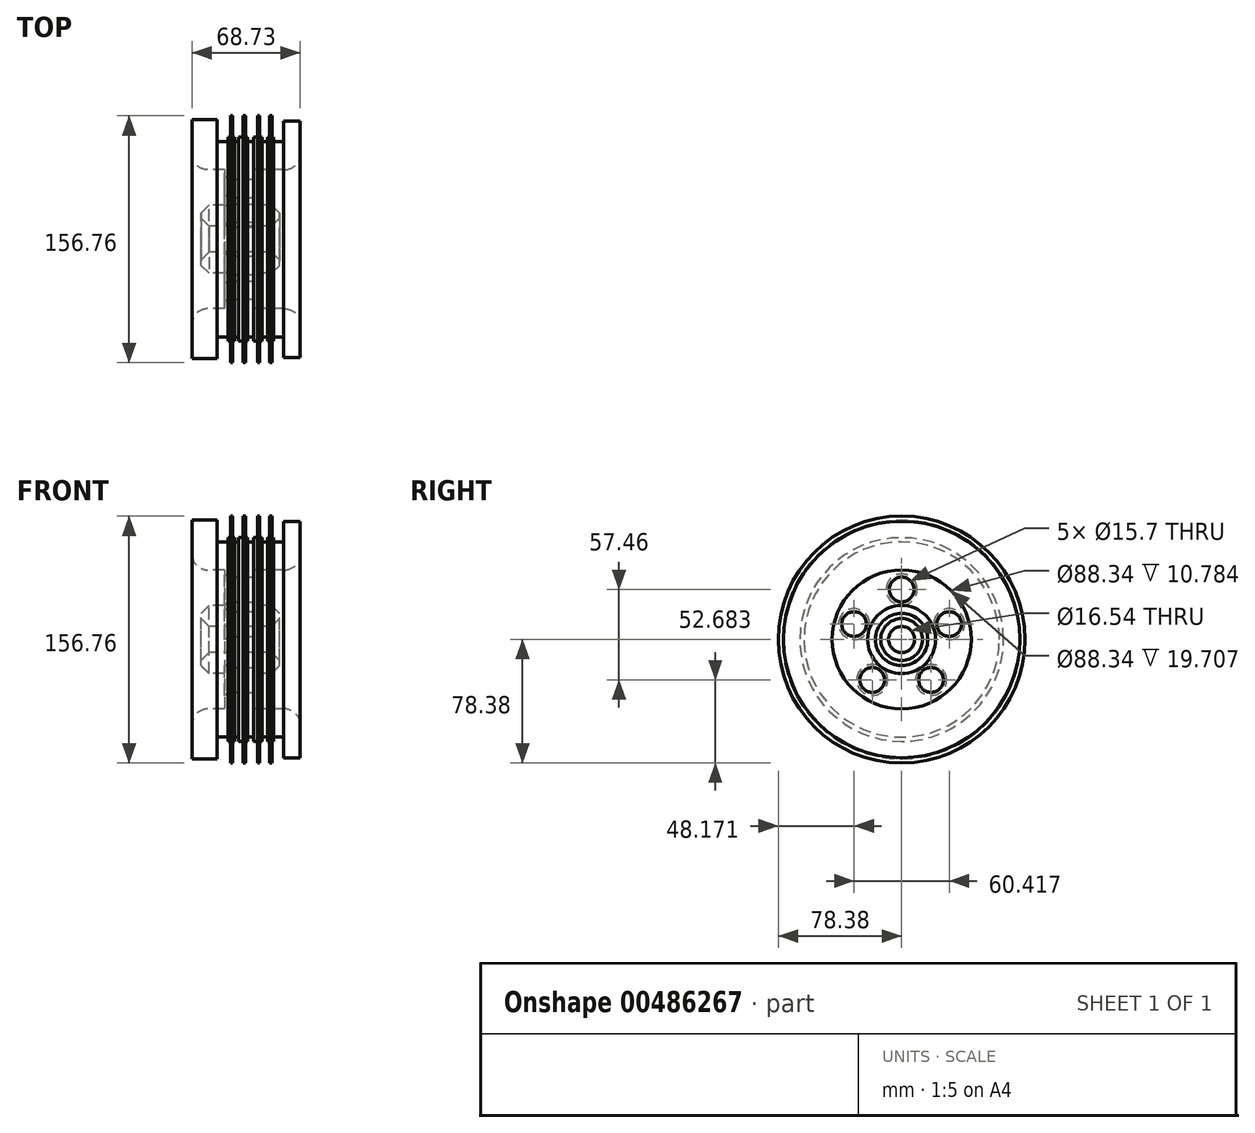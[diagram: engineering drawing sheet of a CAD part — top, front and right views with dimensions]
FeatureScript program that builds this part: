
annotation { "Feature Type Name" : "Feature", "Feature Type Description" : "" }
export const myFeature = defineFeature(function(context is Context, id is Id, definition is map)
    precondition{}
    {
        {
            var Q0;
            Q0=qCreatedBy(makeId("Front.planeOp"),FACE);
            var sketch = newSketch(context, id + "F0", { "sketchPlane" : qUnion([Q0])});
            skLineSegment(sketch, "E0.bottom", {"start": v(-22.97, 62.02) * mm, "end": v(-16.24, 62.02) * mm});
            skLineSegment(sketch, "E0.top", {"start": v(-39.02, 44.17) * mm, "end": v(-18.23, 44.17) * mm});
            skLineSegment(sketch, "E0.left", {"start": v(-39.02, 62.02) * mm, "end": v(-39.02, 44.17) * mm});
            skLineSegment(sketch, "E0.right", {"start": v(29.7, 62.02) * mm, "end": v(29.7, 44.17) * mm});
            skLineSegment(sketch, "E1", {"start": v(-18.23, 44.17) * mm, "end": v(-18.23, 21.61) * mm});
            skLineSegment(sketch, "E2", {"start": v(0, 44.17) * mm, "end": v(0, 21.61) * mm});
            skLineSegment(sketch, "E3.bottom", {"start": v(-33.25, 21.61) * mm, "end": v(-18.23, 21.61) * mm});
            skLineSegment(sketch, "E3.top", {"start": v(-33.25, 8.27) * mm, "end": v(16.54, 8.27) * mm});
            skLineSegment(sketch, "E3.left", {"start": v(-33.25, 21.61) * mm, "end": v(-33.25, 8.27) * mm});
            skLineSegment(sketch, "E3.right", {"start": v(16.54, 21.61) * mm, "end": v(16.54, 8.27) * mm});
            skLineSegment(sketch, "E4.trimOffspring", {"start": v(0, 21.61) * mm, "end": v(16.54, 21.61) * mm});
            skLineSegment(sketch, "E5.trimOffspring", {"start": v(0, 44.17) * mm, "end": v(29.7, 44.17) * mm});
            skLineSegment(sketch, "E6", {"start": v(0, 0) * mm, "end": v(27.25, 0) * mm});
            skPoint(sketch, "E7.end.orphan", {"position": v(22.07, 58.12) * mm});
            skPoint(sketch, "E8.end.orphan", {"position": v(23.89, 62.02) * mm});
            skPoint(sketch, "E9.end.orphan", {"position": v(25.86, 58.12) * mm});
            skLineSegment(sketch, "E10", {"start": v(-39.02, 62.02) * mm, "end": v(-39.02, 75.82) * mm});
            skLineSegment(sketch, "E11", {"start": v(-39.02, 75.82) * mm, "end": v(-22.97, 75.82) * mm});
            skLineSegment(sketch, "E12", {"start": v(-22.97, 75.82) * mm, "end": v(-22.97, 62.02) * mm});
            skLineSegment(sketch, "E13", {"start": v(29.7, 62.02) * mm, "end": v(29.7, 75.07) * mm});
            skLineSegment(sketch, "E14", {"start": v(29.7, 75.07) * mm, "end": v(19.07, 75.07) * mm});
            skLineSegment(sketch, "E15", {"start": v(19.07, 75.07) * mm, "end": v(19.07, 62.02) * mm});
            skPoint(sketch, "E16.orphan", {"position": v(20.1, 62.02) * mm});
            skLineSegment(sketch, "E17.top", {"start": v(12.92, 64.7) * mm, "end": v(11.73, 64.7) * mm});
            skLineSegment(sketch, "E17.left", {"start": v(12.92, 62.02) * mm, "end": v(12.92, 64.7) * mm});
            skLineSegment(sketch, "E17.right", {"start": v(8.93, 62.02) * mm, "end": v(8.93, 64.7) * mm});
            skLineSegment(sketch, "E18.top", {"start": v(5.42, 64.7) * mm, "end": v(3.92, 64.7) * mm});
            skLineSegment(sketch, "E18.left", {"start": v(5.42, 62.02) * mm, "end": v(5.42, 64.7) * mm});
            skLineSegment(sketch, "E18.right", {"start": v(0, 62.02) * mm, "end": v(0, 64.7) * mm});
            skLineSegment(sketch, "E19.top", {"start": v(-3.6, 64.7) * mm, "end": v(-4.98, 64.7) * mm});
            skLineSegment(sketch, "E19.left", {"start": v(-3.6, 62.02) * mm, "end": v(-3.6, 64.7) * mm});
            skLineSegment(sketch, "E19.right", {"start": v(-9.3, 62.02) * mm, "end": v(-9.3, 64.7) * mm});
            skLineSegment(sketch, "E20.top", {"start": v(-11.87, 64.7) * mm, "end": v(-13.19, 64.7) * mm});
            skLineSegment(sketch, "E20.left", {"start": v(-11.87, 62.02) * mm, "end": v(-11.87, 64.7) * mm});
            skLineSegment(sketch, "E20.right", {"start": v(-16.24, 62.02) * mm, "end": v(-16.24, 64.7) * mm});
            skLineSegment(sketch, "E21.trimOffspring", {"start": v(12.92, 62.02) * mm, "end": v(19.07, 62.02) * mm});
            skLineSegment(sketch, "E22.trimOffspring", {"start": v(5.42, 62.02) * mm, "end": v(8.93, 62.02) * mm});
            skLineSegment(sketch, "E23.trimOffspring", {"start": v(-3.6, 62.02) * mm, "end": v(0, 62.02) * mm});
            skLineSegment(sketch, "E24.trimOffspring", {"start": v(-11.87, 62.02) * mm, "end": v(-9.3, 62.02) * mm});
            skLineSegment(sketch, "E25.top", {"start": v(11.73, 78.38) * mm, "end": v(10.25, 78.38) * mm});
            skLineSegment(sketch, "E25.left", {"start": v(11.73, 64.7) * mm, "end": v(11.73, 78.38) * mm});
            skLineSegment(sketch, "E25.right", {"start": v(10.25, 64.7) * mm, "end": v(10.25, 78.38) * mm});
            skLineSegment(sketch, "E26.top", {"start": v(3.92, 78.38) * mm, "end": v(2.61, 78.38) * mm});
            skLineSegment(sketch, "E26.left", {"start": v(3.92, 64.7) * mm, "end": v(3.92, 78.38) * mm});
            skLineSegment(sketch, "E26.right", {"start": v(2.61, 64.7) * mm, "end": v(2.61, 78.38) * mm});
            skLineSegment(sketch, "E27.top", {"start": v(-4.98, 78.38) * mm, "end": v(-6.57, 78.38) * mm});
            skLineSegment(sketch, "E27.left", {"start": v(-4.98, 64.7) * mm, "end": v(-4.98, 78.38) * mm});
            skLineSegment(sketch, "E27.right", {"start": v(-6.57, 64.7) * mm, "end": v(-6.57, 78.38) * mm});
            skPoint(sketch, "E28.oppositeSnap0", {"position": v(-5.78, 78.38) * mm});
            skLineSegment(sketch, "E28.top", {"start": v(-13.19, 78.38) * mm, "end": v(-14.52, 78.38) * mm});
            skLineSegment(sketch, "E28.left", {"start": v(-13.19, 64.7) * mm, "end": v(-13.19, 78.38) * mm});
            skLineSegment(sketch, "E28.right", {"start": v(-14.52, 64.7) * mm, "end": v(-14.52, 78.38) * mm});
            skLineSegment(sketch, "E29.trimOffspring", {"start": v(-6.57, 64.7) * mm, "end": v(-9.3, 64.7) * mm});
            skLineSegment(sketch, "E30.trimOffspring", {"start": v(-14.52, 64.7) * mm, "end": v(-16.24, 64.7) * mm});
            skLineSegment(sketch, "E31.trimOffspring", {"start": v(2.61, 64.7) * mm, "end": v(0, 64.7) * mm});
            skLineSegment(sketch, "E32.trimOffspring", {"start": v(10.25, 64.7) * mm, "end": v(8.93, 64.7) * mm});
            skPoint(sketch, "E33.orphan", {"position": v(-13.19, 71.54) * mm});
            skPoint(sketch, "E34.orphan", {"position": v(10.25, 71.54) * mm});
            skSolve(sketch);
        }
        {
            var Q0;
            Q0=makeQuery(id+"F0.imprint","IMPRINT",FACE,{"disambiguationData":[TD([[makeQuery(id+"F0.imprint","IMPRINT",EDGE,{"derivedFrom":sQuery(id+"F0.wireOp",EDGE,"E0.bottom")}),-1.0]])]});
            var Q1;
            Q1=sQuery(id+"F0.wireOp",EDGE,"E6");
            revolve(context, id + "F1", {"entities" : qUnion([Q0]), "axis" : qUnion([Q1]), "revolveType" : RevolveType.FULL});
        }
        {
            var Q0;
            Q0=makeQuery(id+"F1.opRevolve","SWEPT_FACE",FACE,{"disambiguationData":[OSD([sQuery(id+"F0.wireOp",EDGE,"E2")])]});
            var sketch = newSketch(context, id + "F2", { "sketchPlane" : qUnion([Q0])});
            skCircle(sketch, "E35", {"center": v(0, 31.76) * mm, "radius": 7.85 * mm});
            skCircle(sketch, "E36.1.0", {"center": v(-30.2, 9.82) * mm, "radius": 7.85 * mm});
            skCircle(sketch, "E36.2.0", {"center": v(-18.67, -25.7) * mm, "radius": 7.85 * mm});
            skCircle(sketch, "E36.3.0", {"center": v(18.67, -25.7) * mm, "radius": 7.85 * mm});
            skCircle(sketch, "E36.4.0", {"center": v(30.2, 9.82) * mm, "radius": 7.85 * mm});
            skPoint(sketch, "E36.center", {"position": v(0, 0) * mm});
            skSolve(sketch);
        }
        {
            var Q0;
            Q0=makeQuery(id+"F2.imprint","IMPRINT",FACE,{"disambiguationData":[TD([[makeQuery(id+"F2.imprint","IMPRINT",EDGE,{"derivedFrom":sQuery(id+"F2.wireOp",EDGE,"E35")}),1.0]])]});
            var Q1;
            Q1=makeQuery(id+"F2.imprint","IMPRINT",FACE,{"disambiguationData":[TD([[makeQuery(id+"F2.imprint","IMPRINT",EDGE,{"derivedFrom":sQuery(id+"F2.wireOp",EDGE,"E36.4.0")}),1.0]])]});
            var Q2;
            Q2=makeQuery(id+"F2.imprint","IMPRINT",FACE,{"disambiguationData":[TD([[makeQuery(id+"F2.imprint","IMPRINT",EDGE,{"derivedFrom":sQuery(id+"F2.wireOp",EDGE,"E36.3.0")}),1.0]])]});
            var Q3;
            Q3=makeQuery(id+"F2.imprint","IMPRINT",FACE,{"disambiguationData":[TD([[makeQuery(id+"F2.imprint","IMPRINT",EDGE,{"derivedFrom":sQuery(id+"F2.wireOp",EDGE,"E36.2.0")}),1.0]])]});
            var Q4;
            Q4=makeQuery(id+"F2.imprint","IMPRINT",FACE,{"disambiguationData":[TD([[makeQuery(id+"F2.imprint","IMPRINT",EDGE,{"derivedFrom":sQuery(id+"F2.wireOp",EDGE,"E36.1.0")}),1.0]])]});
            extrude(context, id + "F3", {"entities" : qUnion([Q0, Q1, Q2, Q3, Q4]), "operationType" : NewBodyOperationType.REMOVE, "oppositeDirection" : true, "depth" : 25 * mm});
        }
        {
            var Q0;
            Q0=makeQuery(id+"F1.opRevolve","SWEPT_EDGE",EDGE,{"disambiguationData":[OSD([sQuery(id+"F0.wireOp",EDGE,"E0.top"),sQuery(id+"F0.wireOp",EDGE,"E0.left")])]});
            var Q1;
            Q1=makeQuery(id+"F1.opRevolve","SWEPT_EDGE",EDGE,{"disambiguationData":[OSD([sQuery(id+"F0.wireOp",EDGE,"E0.right"),sQuery(id+"F0.wireOp",EDGE,"E5.trimOffspring")])]});
            fillet(context, id + "F4", {"entities" : qUnion([Q0, Q1]), "radius" : 10 * mm, "tangentPropagation" : true, "allowEdgeOverflow" : false});
        }
        {
            var Q0;
            Q0=makeQuery(id+"F1.opRevolve","SWEPT_EDGE",EDGE,{"disambiguationData":[OSD([sQuery(id+"F0.wireOp",EDGE,"E3.right"),sQuery(id+"F0.wireOp",EDGE,"E4.trimOffspring")])]});
            var Q1;
            Q1=makeQuery(id+"F1.opRevolve","SWEPT_EDGE",EDGE,{"disambiguationData":[OSD([sQuery(id+"F0.wireOp",EDGE,"E3.bottom"),sQuery(id+"F0.wireOp",EDGE,"E3.left")])]});
            chamfer(context, id + "F5", {"entities" : qUnion([Q0, Q1]), "width" : 5 * mm, "tangentPropagation" : true});
        }
        {
            var Q0;
            Q0=makeQuery(id+"F1.opRevolve","SWEPT_EDGE",EDGE,{"disambiguationData":[OSD([sQuery(id+"F0.wireOp",EDGE,"E3.top"),sQuery(id+"F0.wireOp",EDGE,"E3.right")])]});
            var Q1;
            Q1=makeQuery(id+"F1.opRevolve","SWEPT_EDGE",EDGE,{"disambiguationData":[OSD([sQuery(id+"F0.wireOp",EDGE,"E3.top"),sQuery(id+"F0.wireOp",EDGE,"E3.left")])]});
            chamfer(context, id + "F6", {"entities" : qUnion([Q0, Q1]), "width" : 5 * mm, "tangentPropagation" : true});
        }
        {
            var Q0;
            Q0=makeQuery(id+"F3.boolean.opBoolean","COPY",EDGE,{"derivedFrom":makeQuery(id+"F3.opExtrude","CAP_EDGE",EDGE,{"disambiguationData":[OSD([sQuery(id+"F2.wireOp",EDGE,"E35")])],"isStart":true})});
            var Q1;
            Q1=makeQuery(id+"F3.boolean.opBoolean","COPY",EDGE,{"derivedFrom":makeQuery(id+"F3.opExtrude","CAP_EDGE",EDGE,{"disambiguationData":[OSD([sQuery(id+"F2.wireOp",EDGE,"E36.4.0")])],"isStart":true})});
            var Q2;
            Q2=makeQuery(id+"F3.boolean.opBoolean","COPY",EDGE,{"derivedFrom":makeQuery(id+"F3.opExtrude","CAP_EDGE",EDGE,{"disambiguationData":[OSD([sQuery(id+"F2.wireOp",EDGE,"E36.3.0")])],"isStart":true})});
            var Q3;
            Q3=makeQuery(id+"F3.boolean.opBoolean","COPY",EDGE,{"derivedFrom":makeQuery(id+"F3.opExtrude","CAP_EDGE",EDGE,{"disambiguationData":[OSD([sQuery(id+"F2.wireOp",EDGE,"E36.2.0")])],"isStart":true})});
            var Q4;
            Q4=makeQuery(id+"F3.boolean.opBoolean","COPY",EDGE,{"derivedFrom":makeQuery(id+"F3.opExtrude","CAP_EDGE",EDGE,{"disambiguationData":[OSD([sQuery(id+"F2.wireOp",EDGE,"E36.1.0")])],"isStart":true})});
            var Q5;
            Q5=makeQuery(id+"F3.boolean.opBoolean","INTERSECT",EDGE,{"derivedFrom":[makeQuery(id+"F1.opRevolve","SWEPT_FACE",FACE,{"disambiguationData":[OSD([sQuery(id+"F0.wireOp",EDGE,"E1")])]}),makeQuery(id+"F3.opExtrude","SWEPT_FACE",FACE,{"disambiguationData":[OSD([sQuery(id+"F2.wireOp",EDGE,"E35")])]})]});
            var Q6;
            Q6=makeQuery(id+"F3.boolean.opBoolean","INTERSECT",EDGE,{"derivedFrom":[makeQuery(id+"F1.opRevolve","SWEPT_FACE",FACE,{"disambiguationData":[OSD([sQuery(id+"F0.wireOp",EDGE,"E1")])]}),makeQuery(id+"F3.opExtrude","SWEPT_FACE",FACE,{"disambiguationData":[OSD([sQuery(id+"F2.wireOp",EDGE,"E36.1.0")])]})]});
            var Q7;
            Q7=makeQuery(id+"F3.boolean.opBoolean","INTERSECT",EDGE,{"derivedFrom":[makeQuery(id+"F1.opRevolve","SWEPT_FACE",FACE,{"disambiguationData":[OSD([sQuery(id+"F0.wireOp",EDGE,"E1")])]}),makeQuery(id+"F3.opExtrude","SWEPT_FACE",FACE,{"disambiguationData":[OSD([sQuery(id+"F2.wireOp",EDGE,"E36.2.0")])]})]});
            var Q8;
            Q8=makeQuery(id+"F3.boolean.opBoolean","INTERSECT",EDGE,{"derivedFrom":[makeQuery(id+"F1.opRevolve","SWEPT_FACE",FACE,{"disambiguationData":[OSD([sQuery(id+"F0.wireOp",EDGE,"E1")])]}),makeQuery(id+"F3.opExtrude","SWEPT_FACE",FACE,{"disambiguationData":[OSD([sQuery(id+"F2.wireOp",EDGE,"E36.3.0")])]})]});
            var Q9;
            Q9=makeQuery(id+"F3.boolean.opBoolean","INTERSECT",EDGE,{"derivedFrom":[makeQuery(id+"F1.opRevolve","SWEPT_FACE",FACE,{"disambiguationData":[OSD([sQuery(id+"F0.wireOp",EDGE,"E1")])]}),makeQuery(id+"F3.opExtrude","SWEPT_FACE",FACE,{"disambiguationData":[OSD([sQuery(id+"F2.wireOp",EDGE,"E36.4.0")])]})]});
            chamfer(context, id + "F7", {"entities" : qUnion([Q0, Q1, Q2, Q3, Q4, Q5, Q6, Q7, Q8, Q9]), "width" : 2 * mm, "tangentPropagation" : true});
        }
    });
